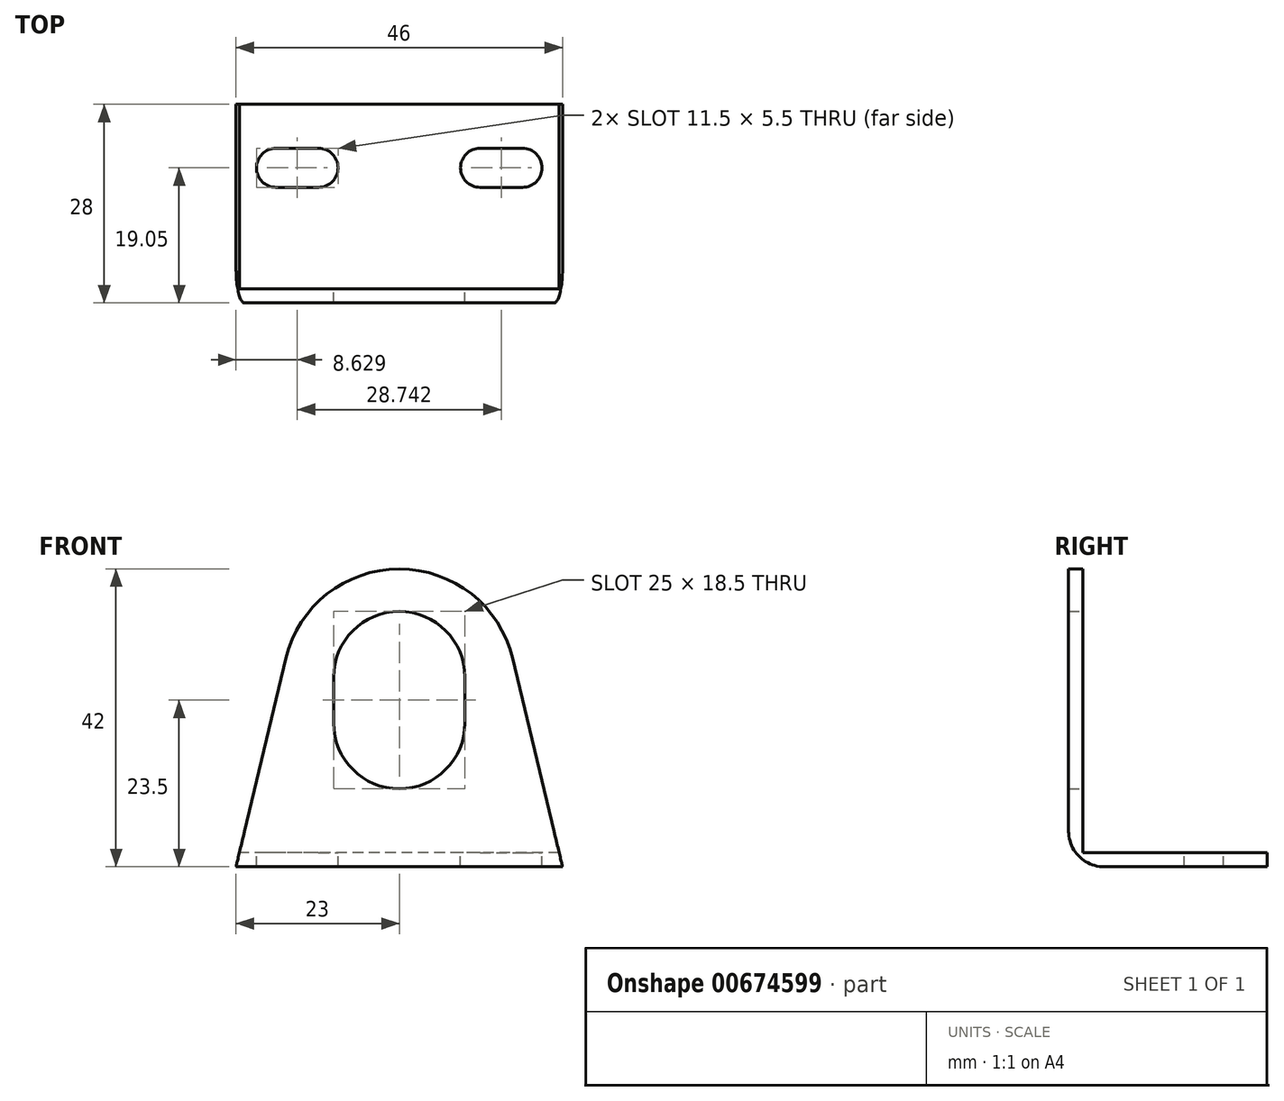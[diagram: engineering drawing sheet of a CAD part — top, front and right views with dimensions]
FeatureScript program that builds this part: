
annotation { "Feature Type Name" : "Feature", "Feature Type Description" : "" }
export const myFeature = defineFeature(function(context is Context, id is Id, definition is map)
    precondition{}
    {
        {
            var Q0;
            Q0=qCreatedBy(makeId("Front.planeOp"),FACE);
            var sketch = newSketch(context, id + "F0", { "sketchPlane" : qUnion([Q0])});
            skLineSegment(sketch, "E0", {"start": v(-23, 0) * mm, "end": v(23, 0) * mm});
            skLineSegment(sketch, "E1", {"start": v(23, 0) * mm, "end": v(15.96, 29.41) * mm});
            skLineSegment(sketch, "E2", {"start": v(-23, 0) * mm, "end": v(-15.96, 29.41) * mm});
            skArc(sketch, "E3", {"start": v(15.96, 29.41) * mm, "mid": v(0, 42) * mm, "end": v(-15.96, 29.41) * mm});
            skLineSegment(sketch, "E4", {"start": v(-9.25, 26.75) * mm, "end": v(-9.25, 20.25) * mm});
            skLineSegment(sketch, "E5", {"start": v(9.25, 26.75) * mm, "end": v(9.25, 20.25) * mm});
            skArc(sketch, "E6", {"start": v(-9.25, 20.25) * mm, "mid": v(0, 11) * mm, "end": v(9.25, 20.25) * mm});
            skArc(sketch, "E7", {"start": v(9.25, 26.75) * mm, "mid": v(0, 36) * mm, "end": v(-9.25, 26.75) * mm});
            skPoint(sketch, "E8", {"position": v(0, 0) * mm});
            skPoint(sketch, "E9", {"position": v(0, 42) * mm});
            skSolve(sketch);
        }
        {
            var Q0;
            Q0=qSketchRegion(id+"F0",true);
            extrude(context, id + "F1", {"entities" : qUnion([Q0]), "depth" : 2 * mm, "offsetDistance" : 25 * mm});
        }
        {
            var Q0;
            Q0=makeQuery(id+"F1.opExtrude","CAP_FACE",FACE,{"disambiguationData":[OSD([sQuery(id+"F0.wireOp",EDGE,"E0"),sQuery(id+"F0.wireOp",EDGE,"E1"),sQuery(id+"F0.wireOp",EDGE,"E2"),sQuery(id+"F0.wireOp",EDGE,"E3"),sQuery(id+"F0.wireOp",EDGE,"E4"),sQuery(id+"F0.wireOp",EDGE,"E5"),sQuery(id+"F0.wireOp",EDGE,"E6"),sQuery(id+"F0.wireOp",EDGE,"E7")])],"isStart":true});
            var sketch = newSketch(context, id + "F2", { "sketchPlane" : qUnion([Q0])});
            skLineSegment(sketch, "E10", {"start": v(-22.52, 2) * mm, "end": v(22.52, 2) * mm});
            skSolve(sketch);
        }
        {
            var Q0;
            {var subQ0=sQuery(id+"F2.wireOp",EDGE,"E10");Q0=makeQuery(id+"F2.imprint","IMPRINT",FACE,{"disambiguationData":[TD([[makeQuery(id+"F2.imprint","IMPRINT",EDGE,{"derivedFrom":subQ0}),-1.0]])]});}
            extrude(context, id + "F3", {"entities" : qUnion([Q0]), "operationType" : NewBodyOperationType.ADD, "depth" : 26 * mm, "offsetDistance" : 25 * mm});
        }
        {
            var Q0;
            Q0=makeQuery(id+"F1.opExtrude","CAP_EDGE",EDGE,{"disambiguationData":[OSD([sQuery(id+"F0.wireOp",EDGE,"E0")])],"isStart":false});
            var Q1;
            Q1=makeQuery(id+"F3.opExtrude","CAP_EDGE",EDGE,{"disambiguationData":[OSD([sQuery(id+"F2.wireOp",EDGE,"E10")])],"isStart":true});
            fillet(context, id + "F4", {"entities" : qUnion([Q0, Q1]), "radius" : 5 * mm, "tangentPropagation" : true, "allowEdgeOverflow" : false});
        }
        {
            var Q0;
            Q0=makeQuery(id+"F3.opExtrude","SWEPT_FACE",FACE,{"disambiguationData":[OSD([sQuery(id+"F2.wireOp",EDGE,"E10")])]});
            var sketch = newSketch(context, id + "F5", { "sketchPlane" : qUnion([Q0])});
            skLineSegment(sketch, "E11.bottom", {"start": v(11.37, 19.8) * mm, "end": v(17.37, 19.8) * mm});
            skLineSegment(sketch, "E11.top", {"start": v(11.37, 14.3) * mm, "end": v(17.37, 14.3) * mm});
            skLineSegment(sketch, "E12", {"start": v(0, 26) * mm, "end": v(0, 5) * mm, "construction": true});
            skArc(sketch, "E13", {"start": v(17.37, 14.3) * mm, "mid": v(20.12, 17.05) * mm, "end": v(17.37, 19.8) * mm});
            skArc(sketch, "E14", {"start": v(11.37, 19.8) * mm, "mid": v(8.62, 17.05) * mm, "end": v(11.37, 14.3) * mm});
            skLineSegment(sketch, "E15.MirrorCS", {"start": v(-11.37, 14.3) * mm, "end": v(-17.37, 14.3) * mm});
            skLineSegment(sketch, "E16.MirrorCS", {"start": v(-11.37, 19.8) * mm, "end": v(-17.37, 19.8) * mm});
            skArc(sketch, "E17.MirrorCS", {"start": v(-17.37, 14.3) * mm, "mid": v(-20.12, 17.05) * mm, "end": v(-17.37, 19.8) * mm});
            skArc(sketch, "E18.MirrorCS", {"start": v(-11.37, 19.8) * mm, "mid": v(-8.62, 17.05) * mm, "end": v(-11.37, 14.3) * mm});
            skSolve(sketch);
        }
        {
            var Q0;
            Q0 = qSketchRegion(id + "F5", true);
            extrude(context, id + "F6", {"entities" : qUnion([Q0]), "operationType" : NewBodyOperationType.REMOVE, "endBound" : BoundingType.THROUGH_ALL, "oppositeDirection" : true, "depth" : 25 * mm, "offsetDistance" : 25 * mm});
        }
    });
